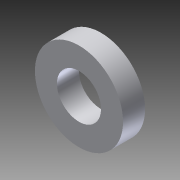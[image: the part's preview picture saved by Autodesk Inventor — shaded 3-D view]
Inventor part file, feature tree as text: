
AUTODESK INVENTOR PART (.ipt)
format: ipt  version: 2012 (Build 160160000, 160)  size: 79,872 bytes
history: native  units: in
note: dims shown in document units (in); Inventor stores cm internally (conversion verified against a paired STEP export)
features: extrude x1, sketch x1
ambient origin geometry x8: Origin, YZ Plane, XZ Plane, XY Plane, X Axis, Y Axis, Z Axis, Center Point
bodies: Solid1 (feature_tree)
feature tree (2):
  extrude  "Extrusion1"  Depth=0.5in
  sketch  "Sketch1"  dims[d0=0.25in d1=0.5in d2=0.125in d3=0.0in]
